# Revit family: Profile_Plastic-Components_Casing-Beads_Corner-Beads
name_source: partatom
category: Profiles
units: mm (PartAtom-declared; Revit-internal decimal feet)

## family parameters
Profile Usage = <Generic>
Rotate with component = No
Section Shape = Not Defined

## types (7) — shared parameters
Assembly Code = C3020800
Construction Details = http://www.arcat.com
Green Building-LEED = http://www.arcat.com
Installation Phase = Stucco Underlayment
Installation-Fabrication = http://www.plasticomponents.com
Keynote = 09 22 36
Manufacturer = Plastic Components, Inc.
Manufacturer Fax = 305-887-2452
Manufacturer Website = www.plasticcomponents.com
Product Data = http://www.arcat.com
Product Properties = http://www.plasticomponents.com
Sales Information = http://www.plasticomponents.com
Specification = http://www.arcat.com
Test Data = http://www.plasticomponents.com
URL = www.plasticcomponents.com
zero-valued in all types: Expected Lifespan (Years), Maintenance Schedule (Months), Warranty Duration (Years)

## per-type parameters (varying)
| type | A | B |
| Profile_Plastic-Components_Casing-Beads_Corner-Beads_BN1A | 0' - 2 1/2" | 0' - 2 1/2" |
| Profile_Plastic-Components_Casing-Beads_Corner-Beads_1A135 | 0' - 2 1/2" | 0' - 2 1/2" |
| Profile_Plastic-Components_Casing-Beads_Corner-Beads_1A4 | 0' - 4" | 0' - 4" |
| Profile_Plastic-Components_Casing-Beads_Corner-Beads_3 | 0' - 2 1/2" | 0' - 1 1/2" |
| Profile_Plastic-Components_Casing-Beads_Corner-Beads_2 | 0' - 2 3/4" | 0' - 2 3/4" |
| Profile_Plastic-Components_Casing-Beads_Corner-Beads_1B | 0' - 1 1/2" | 0' - 1 1/2" |
| Profile_Plastic-Components_Casing-Beads_Corner-Beads_1A | 0' - 2 1/2" | 0' - 2 1/2" |

note: column(s) folded — value = type name in every type: Description, Model

## geometry (parser evidence)
native form markers: Sweep x1
no freeform markers — native parametric forms only
